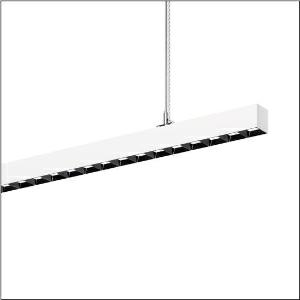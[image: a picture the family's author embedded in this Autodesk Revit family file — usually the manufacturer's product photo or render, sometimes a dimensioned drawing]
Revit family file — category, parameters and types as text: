
# Revit family: silica_r__21_51mx34dc4dwb_1888
name_source: partatom
category: Lighting Fixtures
units: mm (PartAtom-declared; Revit-internal decimal feet)

## family parameters
Cut with Voids When Loaded = No
Host = Face
Light Source = No
Part Type = Normal
Room Calculation Point = No
Round Connector Dimension = Use Diameter
Shared = No

## types (1)
- --- (1 x LED, 19200 lm, 120.3 W, 4000K)
    Apparent Load = 120 VA
    CIE Flux Codes = 74 94 99 56 100
    Color Rendering = 80
    Color Temperature = 4000K
    Default Elevation = 1800 mm
    Description = Silica® 21, office luminaire, primary light control with darklight reflector, of PMMA, black, light emission: direct/indirect distribution, primary light characteristic: asymmetric, installation type: suspended mounting, LED, rated luminous flux: 19.200lm, luminous efficacy: 160lm/W, light colour: 840, colour temperature: 4000K, with terminal, 3+2-pole, max. 2.5mm², mains connection: 220..240V, AC, 50/60Hz, rated input power: 120.3W, luminaire housing, of aluminium, traffic white (RAL 9016), length: 3.004mm, width: 53mm, height: 53mm, protection rating (complete): IP20, insulation class (complete): insulation class I (protective earthing), certification: CE, permissible operating ambient temperature: 0..+35°C, standard: EN 50419, packaging unit: 1 piece
    Height = 53 mm
    Lamp = 1 x LED
    Lamp Light Flux = 19200 lm
    Lamp Power = 120.3 W
    Lamp count = 1
    Length = 3004 mm
    Luminous efficacy = 160 lm/W
    Manufacturer = Siteco
    ModVariant = No
    Model = 51MX34DC4DWB
    Mounting Place = Ceiling
    Mounting Type = Pendant
    Number of Poles = 1
    OnlyDefault = Yes
    Power Factor = 1
    Product Name = Silica® 21
    Product group = office luminaire | ceiling pendant
    ProductGroupID = 902
    Protection Class = Protection class I
    Protection Degree = IP 20
    RLX_Detail_Level = 1
    RLX_Emergency_Light_Flux = 0 lm
    RLX_Emergency_Type = 0
    RLX_Emergency_Type_DB = No
    RlxData = <blob elided: 66765 chars, md5=522c597a>
    Socket = socket
    Standby Power = 0 W
    System Light Flux = 19200 lm
    System Power = 120 W
    Type Comments = factory setting: luminous flux: 100 % | dim-lin: 254 | 418 mA
    Type Image = l_1313619.jpg
    URL = http://relux.com
    VarID = @adj_069157
    Voltage = 0 V
    Weight = 0.00 kg
    Width = 53 mm

## geometry (parser evidence)
native form markers: Blend x4, Sweep x12
no freeform markers — native parametric forms only
